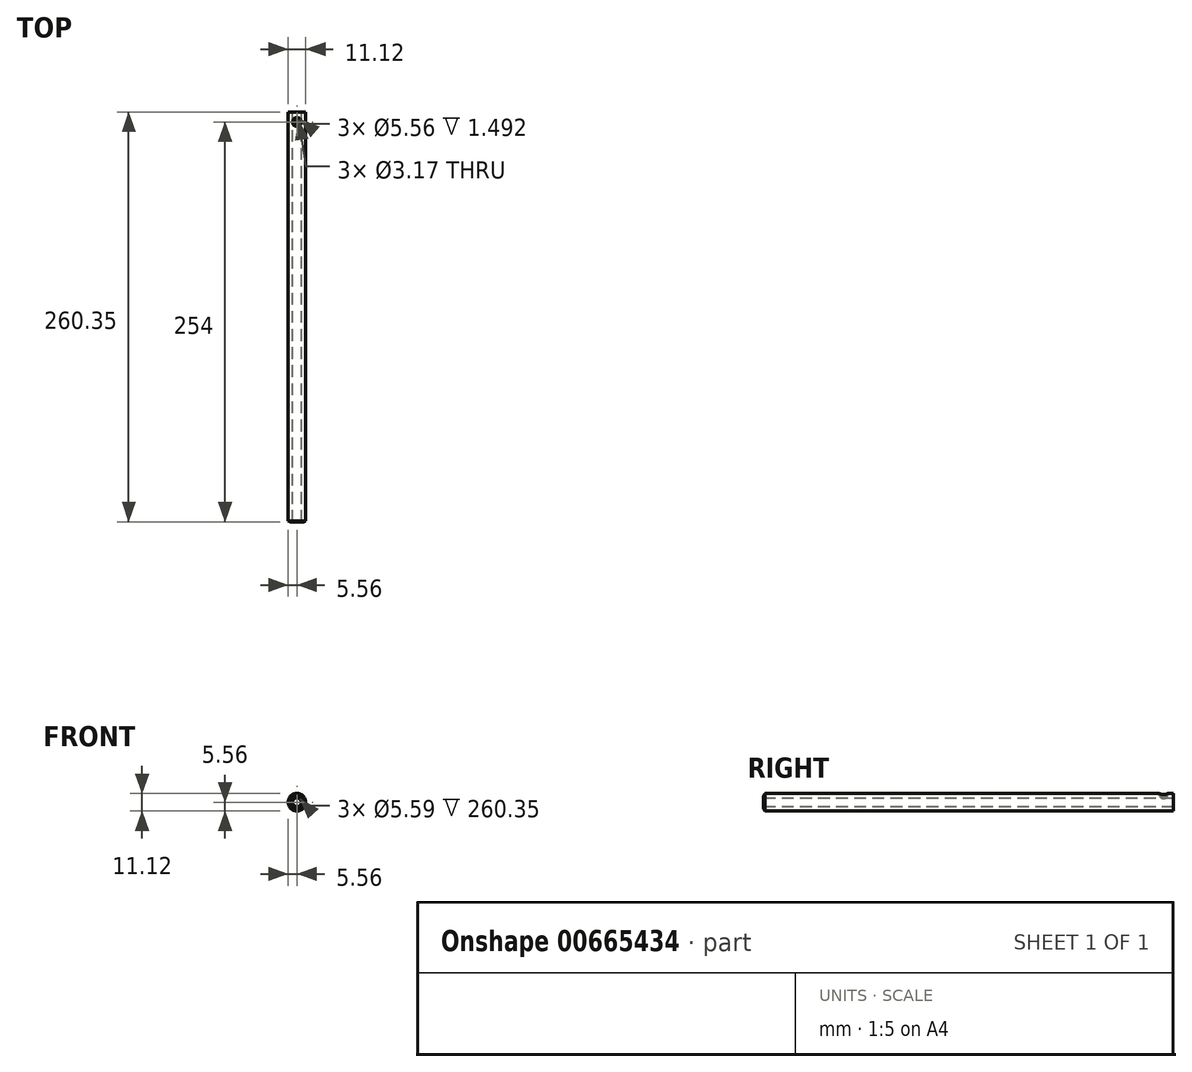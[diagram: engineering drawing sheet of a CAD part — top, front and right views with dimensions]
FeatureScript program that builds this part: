
annotation { "Feature Type Name" : "Feature", "Feature Type Description" : "" }
export const myFeature = defineFeature(function(context is Context, id is Id, definition is map)
    precondition{}
    {
        {
            var Q0;
            Q0=qCreatedBy(makeId("Front.planeOp"),FACE);
            var sketch = newSketch(context, id + "F0", { "sketchPlane" : qUnion([Q0])});
            skCircle(sketch, "E0", {"center": v(0, 0) * mm, "radius": 2.8 * mm});
            skCircle(sketch, "E1", {"center": v(0, 0) * mm, "radius": 5.56 * mm});
            skSolve(sketch);
        }
        {
            var Q0;
            Q0=makeQuery(id+"F0.imprint","IMPRINT",FACE,{"disambiguationData":[TD([[makeQuery(id+"F0.imprint","IMPRINT",EDGE,{"derivedFrom":sQuery(id+"F0.wireOp",EDGE,"E0")}),-1.0]])]});
            extrude(context, id + "F1", {"entities" : qUnion([Q0]), "depth" : 260.35 * mm, "offsetDistance" : 25.4 * mm});
        }
        {
            var Q0;
            Q0=qCreatedBy(makeId("Top.planeOp"),FACE);
            cPlane(context, id + "F2", {"entities" : qUnion([Q0]), "cplaneType" : CPlaneType.OFFSET, "offset" : 6.35 * mm, "width" : 152.4 * mm, "height" : 152.4 * mm});
        }
        {
            var Q0;
            Q0=qCreatedBy(id+"F2.planeOp",FACE);
            var sketch = newSketch(context, id + "F3", { "sketchPlane" : qUnion([Q0])});
            skCircle(sketch, "E2", {"center": v(0, -6.35) * mm, "radius": 2.78 * mm});
            skSolve(sketch);
        }
        {
            var Q0;
            Q0 = qSketchRegion(id + "F3", true);
            extrude(context, id + "F4", {"entities" : qUnion([Q0]), "operationType" : NewBodyOperationType.REMOVE, "oppositeDirection" : true, "depth" : 2.3 * mm, "offsetDistance" : 25.4 * mm});
        }
        {
            var Q0;
            Q0=makeQuery(id+"F4.boolean.opBoolean","COPY",FACE,{"derivedFrom":makeQuery(id+"F4.opExtrude","CAP_FACE",FACE,{"disambiguationData":[OSD([sQuery(id+"F3.wireOp",EDGE,"E2")])],"isStart":false})});
            var sketch = newSketch(context, id + "F5", { "sketchPlane" : qUnion([Q0])});
            skCircle(sketch, "E3", {"center": v(0, -6.35) * mm, "radius": 1.59 * mm});
            skSolve(sketch);
        }
        {
            var Q0;
            Q0 = qSketchRegion(id + "F5", true);
            extrude(context, id + "F6", {"entities" : qUnion([Q0]), "operationType" : NewBodyOperationType.REMOVE, "oppositeDirection" : true, "depth" : 2.3 * mm, "offsetDistance" : 25.4 * mm});
        }
        {
            var Q0;
            Q0=qCreatedBy(makeId("Top.planeOp"),FACE);
            var sketch = newSketch(context, id + "F7", { "sketchPlane" : qUnion([Q0])});
            skLineSegment(sketch, "E4", {"start": v(0, -260.48) * mm, "end": v(0, -256.12) * mm});
            skLineSegment(sketch, "E5", {"start": v(3.9, -260.48) * mm, "end": v(6.38, -259.2) * mm});
            skLineSegment(sketch, "E6", {"start": v(6.38, -259.2) * mm, "end": v(6.38, -261.02) * mm});
            skLineSegment(sketch, "E7", {"start": v(6.38, -261.02) * mm, "end": v(3.9, -260.48) * mm});
            skSolve(sketch);
        }
        {
            var Q0;
            Q0=makeQuery(id+"F7.imprint","IMPRINT",FACE,{"disambiguationData":[TD([[makeQuery(id+"F7.imprint","IMPRINT",EDGE,{"derivedFrom":sQuery(id+"F7.wireOp",EDGE,"E5")}),-1.0]])]});
            var Q1;
            Q1=sQuery(id+"F7.wireOp",EDGE,"E4");
            revolve(context, id + "F8", {"operationType" : NewBodyOperationType.REMOVE, "entities" : qUnion([Q0]), "axis" : qUnion([Q1]), "revolveType" : RevolveType.FULL, "oppositeDirection" : true});
        }
    });
